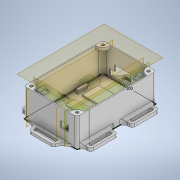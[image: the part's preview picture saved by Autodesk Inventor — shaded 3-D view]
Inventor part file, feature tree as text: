
AUTODESK INVENTOR PART (.ipt)
format: ipt  version: 2021 (Build 250183000, 183)  size: 633,856 bytes
history: native  units: in
note: dims shown in document units (in); Inventor stores cm internally (conversion verified against a paired STEP export)
features: extrude x26, sketch x25, mirror x9, fillet x7, plane x6, chamfer x2, reference x2, other x2
ambient origin geometry x8: Origin, YZ Plane, XZ Plane, XY Plane, X Axis, Y Axis, Z Axis, Center Point
bodies: Solid1 (feature_tree)
feature tree (79):
  sketch  "Sketch1"  dims[d0=3.937in d1=5.9055in]
  extrude  "Extrusion1"  Depth=5.9055in
  extrude  "Extrusion2"  Depth=2.1654in TaperAngle=0.0deg
  sketch  "Sketch2"  dims[d2=0.0787in d3=2.1654in d4=0.0in]
  plane  "Work Plane1"
  extrude  "Extrusion3"  [1 undecoded]
  plane  "Work Plane3"
  plane  "Work Plane4"
  extrude  "Extrusion21"  Depth=1.2598in
  extrude  "Extrusion6"  Depth=0.7087in
  extrude  "Extrusion7"  Depth=2.8346in
  extrude  "Extrusion8"  Depth=0.7874in
  mirror  "Mirror1"
  plane  "Work Plane5"
  extrude  "Extrusion9"  Depth=1.378in
  extrude  "Extrusion10"  Depth=0.0906in
  extrude  "Extrusion11"  Depth=0.0866in
  chamfer  "Chamfer1"  Distance=0.5933in
  extrude  "Extrusion14"  Depth=0.5933in TaperAngle=0.0deg
  extrude  "Extrusion15"  Depth=0.7874in
  extrude  "Extrusion16"  Depth=0.4606in
  plane  "Work Plane7"
  mirror  "Mirror2"
  extrude  "Extrusion17"  Depth=0.5933in TaperAngle=0.0deg
  plane  "Work Plane8"
  extrude  "Extrusion19"  Depth=0.0866in
  mirror  "Mirror3"
  mirror  "Mirror4"
  fillet  "Fillet1"  Radius=0.3236in
  extrude  "Extrusion20"  Depth=0.4724in
  fillet  "Fillet2"  Radius=0.5933in
  mirror  "Mirror5"
  extrude  "Extrusion22"  Depth=0.5906in
  fillet  "Fillet3"  Radius=0.3937in
  mirror  "Mirror6"
  mirror  "Mirror7"
  extrude  "Extrusion23"  Depth=0.1496in
  extrude  "Extrusion24"  Depth=0.0906in
  extrude  "Extrusion25"  Depth=0.1969in
  sketch  "Sketch43"  dims[d85=0.3937in d86=0.5906in d87=0.3937in]
  extrude  "Extrusion26"  Depth=0.2362in TaperAngle=0.0deg
  extrude  "Extrusion27"  TaperAngle=0.0deg  [1 undecoded]
  extrude  "Extrusion28"  Depth=0.1969in TaperAngle=0.0deg
  extrude  "Extrusion29"  Depth=0.0157in
  extrude  "Extrusion30"  Depth=0.0157in
  extrude  "Extrusion31"  Depth=0.9055in
  mirror  "Mirror8"
  mirror  "Mirror9"
  chamfer  "Chamfer2"  Distance=0.9055in
  fillet  "Fillet4"  [1 undecoded]
  fillet  "Fillet5"  Radius=1.8898in
  fillet  "Fillet6"  Radius=1.6535in
  fillet  "Fillet7"  Radius=0.2756in
  sketch  "Sketch6"  dims[d5=0.0787in d6=0.0in d7=-1.5748in]
  sketch  "Sketch11"  dims[d15=1.378in d16=1.2598in]
  sketch  "Sketch13"  dims[d17=1.0236in d18=0.7087in]
  sketch  "Sketch19"  dims[d19=0.1181in d20=0.0in d21=2.8346in]
  sketch  "Sketch20"  dims[d22=0.7087in d31=3.0in d42=0.7874in]
  sketch  "Sketch27"  dims[d43=0.4606in d44=1.378in]
  sketch  "Sketch29"  dims[d45=0.0906in d46=0.3819in]
  sketch  "Sketch30"  dims[d47=0.5933in d48=0.0in d49=0.0866in]
  sketch  "Sketch31"  dims[d50=0.4409in]
  sketch  "Sketch35"  dims[d51=0.3236in d52=0.5933in d53=0.0in]
  sketch  "Sketch36"  dims[d54=0.4724in d55=0.5933in d56=0.0in]
  sketch  "Sketch37"  dims[d57=0.1575in d58=0.0787in d59=45.0deg d63=0.7874in]
  reference  "Reference17"
  sketch  "Sketch38"  dims[d64=0.0906in d65=0.4606in]
  sketch  "Sketch39"  dims[d66=1.378in d67=0.5933in d68=0.0in]
  sketch  "Sketch40"  dims[d69=0.0866in d70=0.4409in d71=0.3236in]
  sketch  "Sketch42"  dims[d72=0.5933in d73=0.0in d74=0.4724in d75=0.5933in d76=0.0in]
  reference  "Reference21"
  sketch  "Sketch44"  dims[d88=0.2697in d89=0.0in d90=0.1496in]
  sketch  "Sketch45"  dims[d91=0.0591in d92=0.0in d93=0.0906in]
  sketch  "Sketch46"  dims[d94=0.1969in d95=0.0in d96=0.689in]
  sketch  "Sketch47"  dims[d98=0.5512in d99=0.2362in d100=0.0in]
  sketch  "Sketch48"  dims[d106=0.1299in d107=0.0in d108=0.0in]
  sketch  "Sketch49"  dims[d109=0.1969in d110=0.1969in d111=0.0in d112=0.0157in d113=0.0157in d114=0.9055in d115=0.9055in d116=0.0in d117=1.8898in d120=1.6535in d121=0.2756in d122=0.1969in d123=0.2362in d124=1.6929in d125=0.1969in d126=2.0866in d127=0.3937in d129=0.2756in d130=0.1969in d131=0.2362in d132=0.0in d133=0.1969in d136=0.315in d137=0.315in d138=2.3622in d139=0.1969in d140=4.1126in d141=0.1752in d142=0.0in d143=0.1728in d144=0.1728in d145=0.0591in d146=0.0in d147=0.0197in d148=0.1181in d149=0.7874in d150=0.315in d151=0.0in d152=0.0591in d153=0.0in d154=0.315in d155=0.315in d156=0.9843in d157=0.7874in d158=0.2697in d159=0.0in d160=0.0906in d161=0.0906in d162=0.2362in d163=0.0in d164=0.1705in d165=0.1705in d166=0.0787in d167=0.0in d168=0.0917in d169=0.0917in d170=0.2362in d171=0.0in d172=0.2362in d173=0.1063in d174=0.0in d175=0.1575in d176=0.1969in d177=0.0787in d178=45.0deg d179=0.315in d180=0.315in d181=0.1969in d182=0.7874in d183=0.1969in]
  other  "Chestbox_with_electronical_devices.iam"
  other  "ArduinoMega_STEP_AP203:1"
note: 3 required parameter values undecoded (feature->parameter linkage not recoverable at this tier; creation-order binding heuristic only, values carry confidence <= 0.55)
